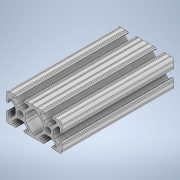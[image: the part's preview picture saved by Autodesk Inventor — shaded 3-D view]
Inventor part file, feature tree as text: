
AUTODESK INVENTOR PART (.ipt)
format: ipt  version: 2020 (Build 240168000, 168)  size: 333,312 bytes
history: native  units: in
note: dims shown in document units (in); Inventor stores cm internally (conversion verified against a paired STEP export)
features: sketch x2, extrude x1
ambient origin geometry x8: Origin, YZ Plane, XZ Plane, XY Plane, X Axis, Y Axis, Z Axis, Center Point
bodies: Solid1 (feature_tree)
feature tree (3):
  extrude  "Extrusion1"  [1 undecoded]
  sketch  "Sketch2"
  sketch  "Sketch1"  dims[d0=4.0in d1=0.0in]
note: 1 required parameter value undecoded (feature->parameter linkage not recoverable at this tier; creation-order binding heuristic only, values carry confidence <= 0.55)
